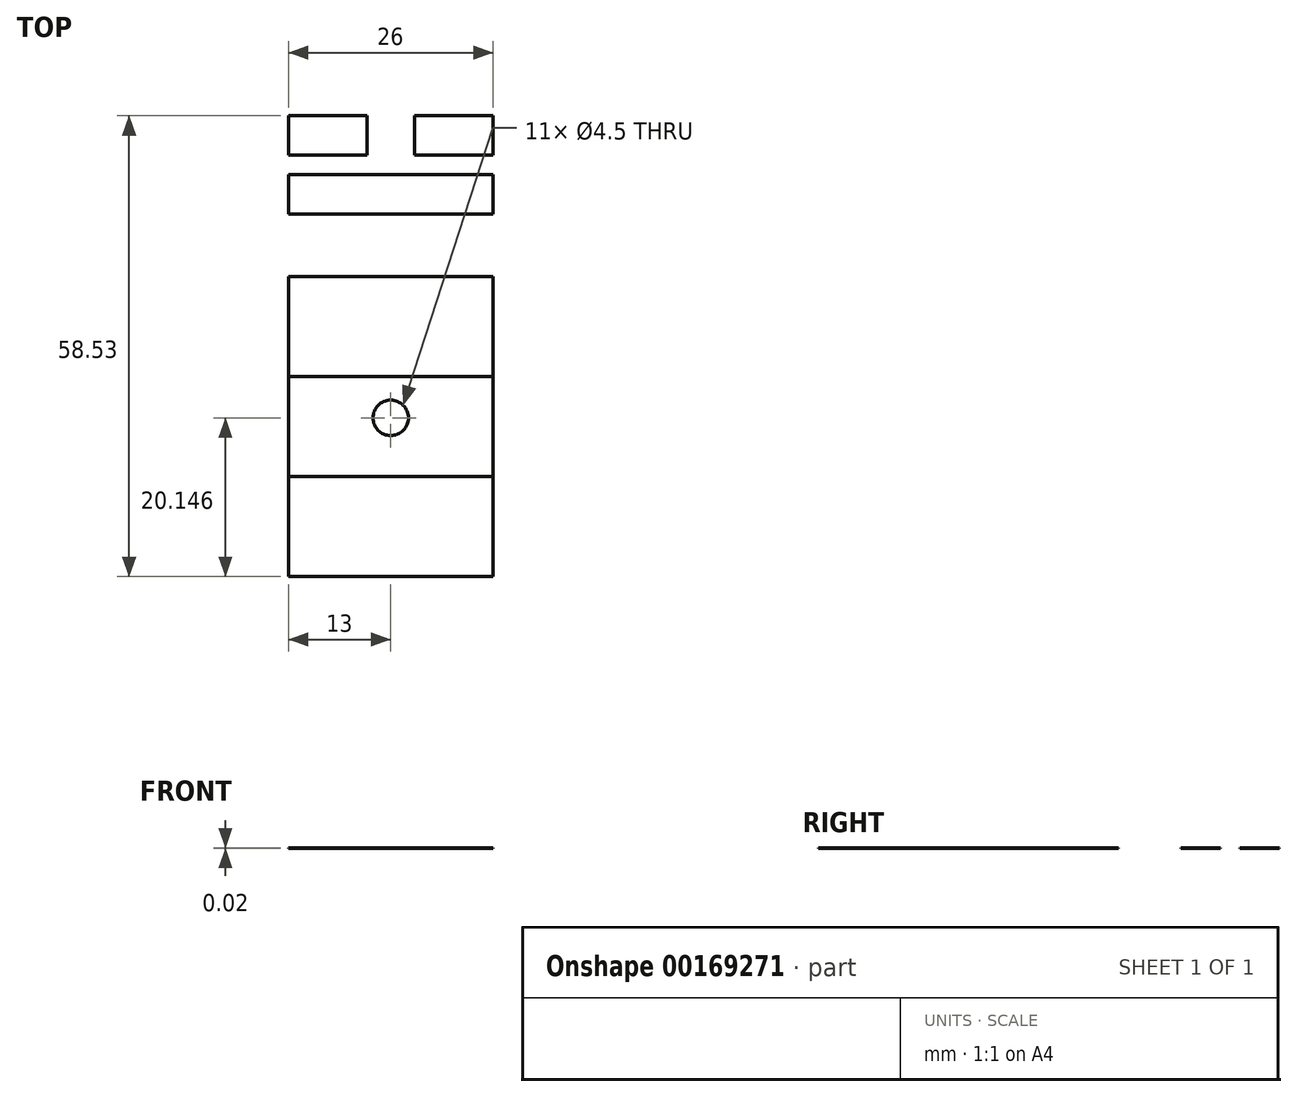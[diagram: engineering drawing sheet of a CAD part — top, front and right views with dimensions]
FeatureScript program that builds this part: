
annotation { "Feature Type Name" : "Feature", "Feature Type Description" : "" }
export const myFeature = defineFeature(function(context is Context, id is Id, definition is map)
    precondition{}
    {
        {
            var Q0;
            Q0=qCreatedBy(makeId("Top.planeOp"),FACE);
            var sketch = newSketch(context, id + "F0", { "sketchPlane" : qUnion([Q0])});
            skLineSegment(sketch, "E0.bottom", {"start": v(13, -6.25) * mm, "end": v(-13, -6.25) * mm});
            skLineSegment(sketch, "E0.top", {"start": v(13, 6.25) * mm, "end": v(-13, 6.25) * mm});
            skLineSegment(sketch, "E0.left", {"start": v(13, -6.25) * mm, "end": v(13, 6.25) * mm});
            skLineSegment(sketch, "E0.right", {"start": v(-13, -6.25) * mm, "end": v(-13, 6.25) * mm});
            skPoint(sketch, "E0.middle", {"position": v(0, 0) * mm});
            skLineSegment(sketch, "E1", {"start": v(-13, 1.25) * mm, "end": v(13, 1.25) * mm});
            skLineSegment(sketch, "E2", {"start": v(13, -1.25) * mm, "end": v(-13, -1.25) * mm});
            skLineSegment(sketch, "E3", {"start": v(-3, 6.25) * mm, "end": v(-3, 1.25) * mm});
            skLineSegment(sketch, "E4", {"start": v(3, 6.25) * mm, "end": v(3, 1.25) * mm});
            skSolve(sketch);
        }
        {
            var Q0;
            Q0 = qSketchRegion(id + "F0", true);
            extrude(context, id + "F1", {"entities" : qUnion([Q0]), "oppositeDirection" : true, "depth" : 1 / 50.8 * mm});
        }
        {
            var Q0;
            {var subQ0=sQuery(id+"F0.wireOp",EDGE,"E3");Q0=makeQuery(id+"F0.imprint","IMPRINT",FACE,{"disambiguationData":[TD([[makeQuery(id+"F0.imprint","IMPRINT",EDGE,{"derivedFrom":subQ0}),1.0]])]});}
            var Q1;
            {var subQ5=sQuery(id+"F0.wireOp",EDGE,"E2");Q1=makeQuery(id+"F0.imprint","IMPRINT",FACE,{"disambiguationData":[TD([[makeQuery(id+"F0.imprint","IMPRINT",EDGE,{"derivedFrom":subQ5}),-1.0]])]});}
            extrude(context, id + "F2", {"entities" : qUnion([Q0, Q1]), "operationType" : NewBodyOperationType.REMOVE, "oppositeDirection" : true, "depth" : 8 * mm});
        }
        {
            var Q0;
            Q0=qCreatedBy(makeId("Top.planeOp"),FACE);
            var sketch = newSketch(context, id + "F3", { "sketchPlane" : qUnion([Q0])});
            skPoint(sketch, "E5.0", {"position": v(-13, 6.25) * mm});
            skPoint(sketch, "E6.0", {"position": v(-3, 6.25) * mm});
            skPoint(sketch, "E7.0", {"position": v(3, 6.25) * mm});
            skPoint(sketch, "E8.0", {"position": v(13, 6.25) * mm});
            skPoint(sketch, "E9", {"position": v(-13, -14.18) * mm});
            skPoint(sketch, "E10", {"position": v(13, -14.18) * mm});
            skLineSegment(sketch, "E11", {"start": v(-13, -14.18) * mm, "end": v(-13, -52.28) * mm});
            skLineSegment(sketch, "E12", {"start": v(-13, -52.28) * mm, "end": v(13, -52.28) * mm});
            skLineSegment(sketch, "E13", {"start": v(13, -52.28) * mm, "end": v(13, -14.18) * mm});
            skLineSegment(sketch, "E14", {"start": v(-13, -14.18) * mm, "end": v(13, -14.18) * mm});
            skLineSegment(sketch, "E15", {"start": v(-13, -26.88) * mm, "end": v(13, -26.88) * mm});
            skLineSegment(sketch, "E16", {"start": v(-13, -39.58) * mm, "end": v(13, -39.58) * mm});
            skPoint(sketch, "E17", {"position": v(0, -32.13) * mm});
            skSolve(sketch);
        }
        {
            var Q0;
            Q0 = qSketchRegion(id + "F3", true);
            extrude(context, id + "F4", {"entities" : qUnion([Q0]), "oppositeDirection" : true, "depth" : 1 / 50.8 * mm});
        }
        {
            var Q0;
            {var subQ0=sQuery(id+"F3.wireOp",EDGE,"E15");Q0=makeQuery(id+"F3.imprint","IMPRINT",FACE,{"disambiguationData":[TD([[makeQuery(id+"F3.imprint","IMPRINT",EDGE,{"derivedFrom":subQ0}),-1.0]])]});}
            extrude(context, id + "F5", {"entities" : qUnion([Q0]), "operationType" : NewBodyOperationType.REMOVE, "oppositeDirection" : true, "depth" : 1 / 101.6 * mm});
        }
        {
            var Q0;
            Q0=sQuery(id+"F3.wireOp",VERTEX,"E17");
            var Q1;
            Q1=makeQuery(id+"F4.opExtrude","SWEPT_BODY",BODY,{"disambiguationData":[OSD([sQuery(id+"F3.wireOp",EDGE,"E11"),sQuery(id+"F3.wireOp",EDGE,"E12"),sQuery(id+"F3.wireOp",EDGE,"E13"),sQuery(id+"F3.wireOp",EDGE,"E14")])]});
            hole(context, id + "F6", {"style" : HoleStyle.SIMPLE, "endStyle" : HoleEndStyle.THROUGH, "holeDiameter" : 4.5 * mm, "startFromSketch" : true, "locations" : qUnion([Q0]), "scope" : qUnion([Q1]), "isTappedThrough" : true});
        }
    });
